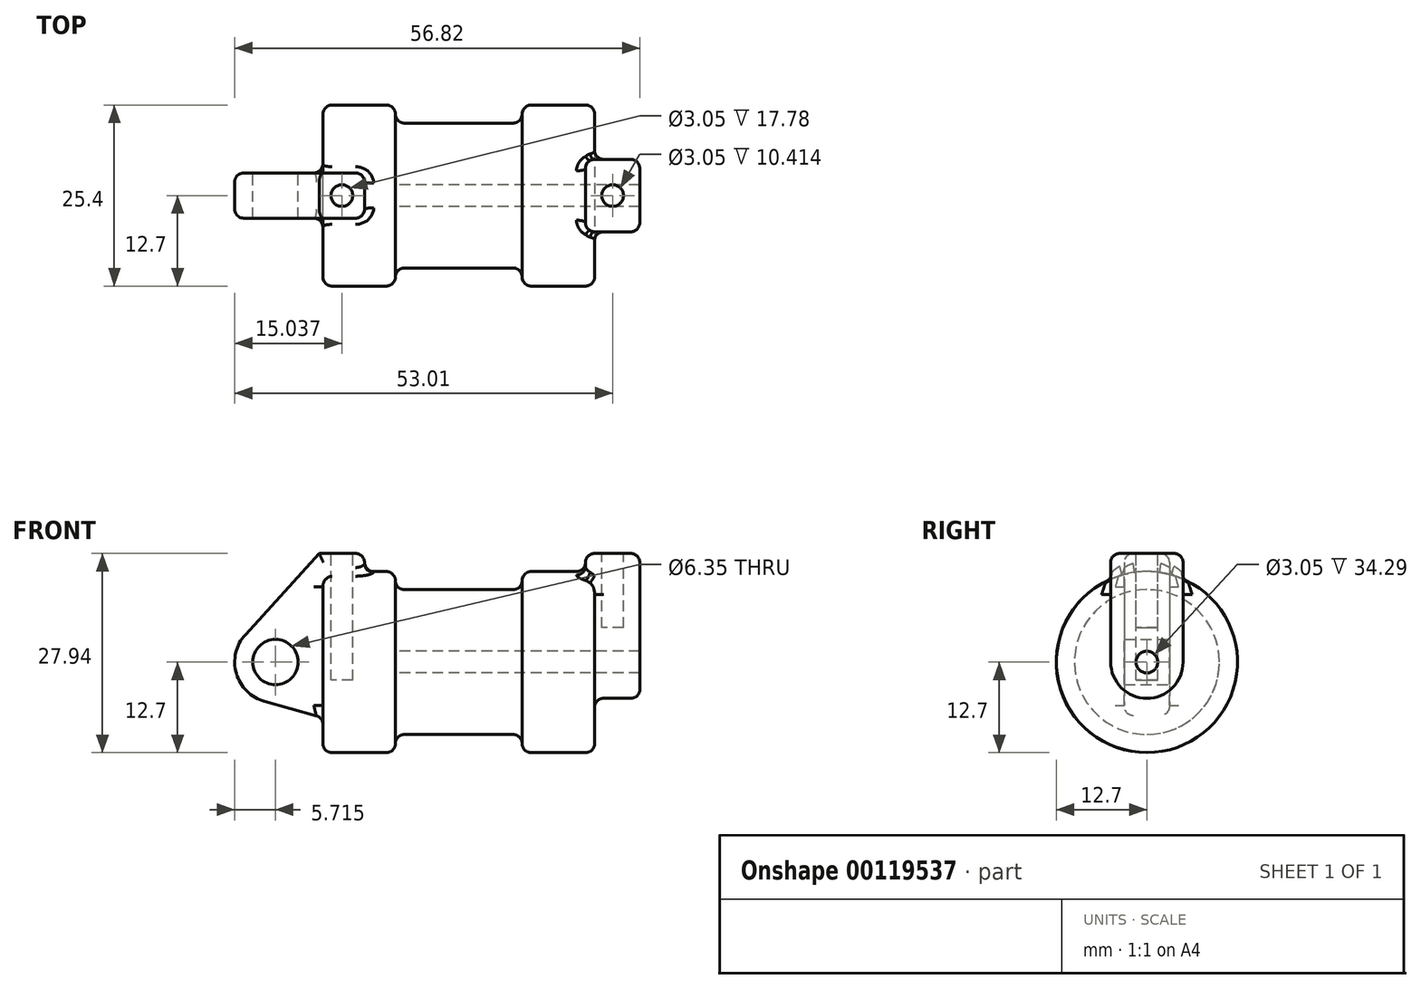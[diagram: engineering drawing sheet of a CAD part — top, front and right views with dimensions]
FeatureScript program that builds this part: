
annotation { "Feature Type Name" : "Feature", "Feature Type Description" : "" }
export const myFeature = defineFeature(function(context is Context, id is Id, definition is map)
    precondition{}
    {
        {
            var Q0;
            Q0=qCreatedBy(makeId("Front.planeOp"),FACE);
            var sketch = newSketch(context, id + "F0", { "sketchPlane" : qUnion([Q0])});
            skLineSegment(sketch, "E0", {"start": v(0, 0) * mm, "end": v(0, 12.7) * mm});
            skLineSegment(sketch, "E1", {"start": v(0, 12.7) * mm, "end": v(10.16, 12.7) * mm});
            skLineSegment(sketch, "E2", {"start": v(10.16, 12.7) * mm, "end": v(10.16, 10.16) * mm});
            skLineSegment(sketch, "E3", {"start": v(10.16, 10.16) * mm, "end": v(27.94, 10.16) * mm});
            skLineSegment(sketch, "E4", {"start": v(27.94, 10.16) * mm, "end": v(27.94, 12.7) * mm});
            skLineSegment(sketch, "E5", {"start": v(27.94, 12.7) * mm, "end": v(38.1, 12.7) * mm});
            skLineSegment(sketch, "E6", {"start": v(38.1, 12.7) * mm, "end": v(38.1, 0) * mm});
            skLineSegment(sketch, "E7", {"start": v(38.1, 0) * mm, "end": v(0, 0) * mm});
            skLineSegment(sketch, "E8", {"start": v(5.84, 15.24) * mm, "end": v(-0.5, 15.24) * mm});
            skLineSegment(sketch, "E9", {"start": v(-0.5, 15.24) * mm, "end": v(-10.88, 3.85) * mm});
            skLineSegment(sketch, "E10", {"start": v(0, 0) * mm, "end": v(-6.65, 0) * mm});
            skCircle(sketch, "E11", {"center": v(-6.65, 0) * mm, "radius": 5.72 * mm});
            skCircle(sketch, "E12", {"center": v(-6.65, 0) * mm, "radius": 3.18 * mm});
            skLineSegment(sketch, "E13", {"start": v(5.84, 15.24) * mm, "end": v(5.84, -9.4) * mm});
            skLineSegment(sketch, "E14", {"start": v(5.84, -9.4) * mm, "end": v(-8.18, -5.5) * mm});
            skSolve(sketch);
        }
        {
            var Q0;
            {var subQ0=sQuery(id+"F0.wireOp",EDGE,"E0");Q0=makeQuery(id+"F0.imprint","IMPRINT",FACE,{"disambiguationData":[TD([[makeQuery(id+"F0.imprint","IMPRINT",EDGE,{"derivedFrom":subQ0}),-1.0]])]});}
            var Q1;
            {var subQ0=sQuery(id+"F0.wireOp",EDGE,"E2");Q1=makeQuery(id+"F0.imprint","IMPRINT",FACE,{"disambiguationData":[TD([[makeQuery(id+"F0.imprint","IMPRINT",EDGE,{"derivedFrom":subQ0}),-1.0]])]});}
            var Q2;
            Q2=sQuery(id+"F0.wireOp",EDGE,"E7");
            revolve(context, id + "F1", {"entities" : qUnion([Q0, Q1]), "axis" : qUnion([Q2]), "revolveType" : RevolveType.FULL});
        }
        {
            var Q0;
            {var subQ4=sQuery(id+"F0.wireOp",EDGE,"E12");Q0=makeQuery(id+"F0.imprint","IMPRINT",FACE,{"disambiguationData":[TD([[makeQuery(id+"F0.imprint","IMPRINT",EDGE,{"derivedFrom":subQ4}),-1.0]])]});}
            var Q1;
            {var subQ0=sQuery(id+"F0.wireOp",EDGE,"E14");Q1=makeQuery(id+"F0.imprint","IMPRINT",FACE,{"disambiguationData":[TD([[makeQuery(id+"F0.imprint","IMPRINT",EDGE,{"derivedFrom":subQ0}),-1.0]])]});}
            var Q2;
            {var subQ3=sQuery(id+"F0.wireOp",EDGE,"E0");Q2=makeQuery(id+"F0.imprint","IMPRINT",FACE,{"disambiguationData":[TD([[makeQuery(id+"F0.imprint","IMPRINT",EDGE,{"derivedFrom":subQ3}),1.0]])]});}
            var Q3;
            {var subQ0=sQuery(id+"F0.wireOp",EDGE,"E0");Q3=makeQuery(id+"F0.imprint","IMPRINT",FACE,{"disambiguationData":[TD([[makeQuery(id+"F0.imprint","IMPRINT",EDGE,{"derivedFrom":subQ0}),-1.0]])]});}
            extrude(context, id + "F2", {"entities" : qUnion([Q0, Q1, Q2, Q3]), "operationType" : NewBodyOperationType.ADD, "endBound" : BoundingType.SYMMETRIC, "depth" : 6.35 * mm});
        }
        {
            var Q0;
            Q0=makeQuery(id+"F1.opRevolve","SWEPT_FACE",FACE,{"disambiguationData":[OSD([sQuery(id+"F0.wireOp",EDGE,"E6")])]});
            var sketch = newSketch(context, id + "F3", { "sketchPlane" : qUnion([Q0])});
            skCircle(sketch, "E15", {"center": v(0, 0) * mm, "radius": 1.52 * mm});
            skCircle(sketch, "E16", {"center": v(0, 0) * mm, "radius": 5.08 * mm});
            skLineSegment(sketch, "E17", {"start": v(-5.08, 0) * mm, "end": v(-5.08, 15.24) * mm});
            skLineSegment(sketch, "E18", {"start": v(-5.08, 15.24) * mm, "end": v(5.08, 15.24) * mm});
            skLineSegment(sketch, "E19", {"start": v(5.08, 15.24) * mm, "end": v(5.08, 0) * mm});
            skSolve(sketch);
        }
        {
            var Q0;
            {var subQ0=sQuery(id+"F3.wireOp",EDGE,"E18");Q0=makeQuery(id+"F3.imprint","IMPRINT",FACE,{"disambiguationData":[TD([[makeQuery(id+"F3.imprint","IMPRINT",EDGE,{"derivedFrom":subQ0}),-1.0]])]});}
            var Q1;
            {var subQ0=sQuery(id+"F3.wireOp",EDGE,"E17");var subQ1=sQuery(id+"F3.wireOp",EDGE,"E16");var subQ2=makeQuery(id+"F3.imprint","INTERSECT",VERTEX,{"derivedFrom":[subQ1,subQ0]});Q1=makeQuery(id+"F3.imprint","IMPRINT",FACE,{"disambiguationData":[TD([[makeQuery(id+"F3.imprint","IMPRINT",EDGE,{"disambiguationData":[TD([[subQ2,1.0]])],"derivedFrom":subQ1}),-1.0]])]});}
            var Q2;
            Q2=makeQuery(id+"F3.imprint","IMPRINT",FACE,{"disambiguationData":[TD([[makeQuery(id+"F3.imprint","IMPRINT",EDGE,{"derivedFrom":sQuery(id+"F3.wireOp",EDGE,"E15")}),-1.0]])]});
            extrude(context, id + "F4", {"entities" : qUnion([Q0, Q1, Q2]), "operationType" : NewBodyOperationType.ADD, "depth" : 6.35 * mm, "hasSecondDirection" : true, "secondDirectionOppositeDirection" : true, "secondDirectionDepth" : 1.27 * mm});
        }
        {
            var Q0;
            Q0=makeQuery(id+"F4.boolean.opBoolean","SPLIT",FACE,{"disambiguationData":[TD([makeQuery(id+"F4.opExtrude","SWEPT_FACE",FACE,{"disambiguationData":[OSD([sQuery(id+"F3.wireOp",EDGE,"E15")])]})])],"derivedFrom":makeQuery(id+"F1.opRevolve","SWEPT_FACE",FACE,{"disambiguationData":[OSD([sQuery(id+"F0.wireOp",EDGE,"E6")])]})});
            var Q1;
            Q1=makeQuery(id+"F1.opRevolve","SWEPT_FACE",FACE,{"disambiguationData":[OSD([sQuery(id+"F0.wireOp",EDGE,"E2")])]});
            extrude(context, id + "F5", {"entities" : qUnion([Q0]), "operationType" : NewBodyOperationType.REMOVE, "endBound" : BoundingType.UP_TO_SURFACE, "oppositeDirection" : true, "endBoundEntityFace" : qUnion([Q1]), "depth" : 25.4 * mm});
        }
        {
            var Q0;
            Q0=makeQuery(id+"F2.opExtrude","SWEPT_FACE",FACE,{"disambiguationData":[OSD([sQuery(id+"F0.wireOp",EDGE,"E8")])]});
            var sketch = newSketch(context, id + "F6", { "sketchPlane" : qUnion([Q0])});
            skLineSegment(sketch, "E20", {"start": v(2.67, 3.18) * mm, "end": v(2.67, -3.18) * mm, "construction": true});
            skLineSegment(sketch, "E21", {"start": v(-0.5, 0) * mm, "end": v(5.84, 0) * mm, "construction": true});
            skCircle(sketch, "E22", {"center": v(2.67, 0) * mm, "radius": 1.52 * mm});
            skSolve(sketch);
        }
        {
            var Q0;
            Q0=makeQuery(id+"F4.opExtrude","SWEPT_FACE",FACE,{"disambiguationData":[OSD([sQuery(id+"F3.wireOp",EDGE,"E18")])]});
            var sketch = newSketch(context, id + "F7", { "sketchPlane" : qUnion([Q0])});
            skLineSegment(sketch, "E23", {"start": v(40.64, 5.08) * mm, "end": v(40.64, -5.08) * mm, "construction": true});
            skLineSegment(sketch, "E24", {"start": v(36.83, 0) * mm, "end": v(44.45, 0) * mm, "construction": true});
            skCircle(sketch, "E25", {"center": v(40.64, 0) * mm, "radius": 1.52 * mm});
            skSolve(sketch);
        }
        {
            var Q0;
            Q0=makeQuery(id+"F6.imprint","IMPRINT",FACE,{"disambiguationData":[TD([[makeQuery(id+"F6.imprint","IMPRINT",EDGE,{"derivedFrom":sQuery(id+"F6.wireOp",EDGE,"E22")}),1.0]])]});
            extrude(context, id + "F8", {"entities" : qUnion([Q0]), "operationType" : NewBodyOperationType.REMOVE, "oppositeDirection" : true, "depth" : 17.78 * mm});
        }
        {
            var Q0;
            Q0=makeQuery(id+"F7.imprint","IMPRINT",FACE,{"disambiguationData":[TD([[makeQuery(id+"F7.imprint","IMPRINT",EDGE,{"derivedFrom":sQuery(id+"F7.wireOp",EDGE,"E25")}),1.0]])]});
            var Q1;
            Q1=sQuery(id+"F7.wireOp",EDGE,"E25");
            extrude(context, id + "F9", {"entities" : qUnion([Q0]), "operationType" : NewBodyOperationType.REMOVE, "surfaceEntities" : qUnion([Q1]), "oppositeDirection" : true, "depth" : 10.4 * mm});
        }
        {
            var Q0;
            Q0=makeQuery(id+"F1.opRevolve","SWEPT_EDGE",EDGE,{"disambiguationData":[OSD([sQuery(id+"F0.wireOp",EDGE,"E4"),sQuery(id+"F0.wireOp",EDGE,"E5")])]});
            var Q1;
            Q1=makeQuery(id+"F1.opRevolve","SWEPT_EDGE",EDGE,{"disambiguationData":[OSD([sQuery(id+"F0.wireOp",EDGE,"E1"),sQuery(id+"F0.wireOp",EDGE,"E2")])]});
            fillet(context, id + "F10", {"entities" : qUnion([Q0, Q1]), "radius" : 1.27 * mm, "tangentPropagation" : true, "allowEdgeOverflow" : false});
        }
        {
            var Q0;
            Q0=makeQuery(id+"F1.opRevolve","SWEPT_EDGE",EDGE,{"disambiguationData":[OSD([sQuery(id+"F0.wireOp",EDGE,"E3"),sQuery(id+"F0.wireOp",EDGE,"E4")])]});
            var Q1;
            Q1=makeQuery(id+"F1.opRevolve","SWEPT_EDGE",EDGE,{"disambiguationData":[OSD([sQuery(id+"F0.wireOp",EDGE,"E2"),sQuery(id+"F0.wireOp",EDGE,"E3")])]});
            fillet(context, id + "F11", {"entities" : qUnion([Q0, Q1]), "radius" : 1.27 * mm, "tangentPropagation" : true, "allowEdgeOverflow" : false});
        }
        {
            var Q0;
            Q0=makeQuery(id+"F1.opRevolve","SWEPT_EDGE",EDGE,{"disambiguationData":[OSD([sQuery(id+"F0.wireOp",EDGE,"E5"),sQuery(id+"F0.wireOp",EDGE,"E6")])]});
            fillet(context, id + "F12", {"entities" : qUnion([Q0]), "radius" : 1.27 * mm, "tangentPropagation" : true, "allowEdgeOverflow" : false});
        }
        {
            var Q0;
            Q0=makeQuery(id+"F1.opRevolve","SWEPT_EDGE",EDGE,{"disambiguationData":[OSD([sQuery(id+"F0.wireOp",EDGE,"E0"),sQuery(id+"F0.wireOp",EDGE,"E1")])]});
            fillet(context, id + "F13", {"entities" : qUnion([Q0]), "radius" : 1.27 * mm, "tangentPropagation" : true, "allowEdgeOverflow" : false});
        }
        {
            var Q0;
            Q0=makeQuery(id+"F4.opExtrude","CAP_EDGE",EDGE,{"disambiguationData":[OSD([sQuery(id+"F3.wireOp",EDGE,"E19")])],"isStart":false});
            var Q1;
            Q1=makeQuery(id+"F4.opExtrude","CAP_EDGE",EDGE,{"disambiguationData":[OSD([sQuery(id+"F3.wireOp",EDGE,"E16")])],"isStart":false});
            var Q2;
            Q2=makeQuery(id+"F4.opExtrude","CAP_EDGE",EDGE,{"disambiguationData":[OSD([sQuery(id+"F3.wireOp",EDGE,"E17")])],"isStart":false});
            var Q3;
            Q3=makeQuery(id+"F4.opExtrude","SWEPT_EDGE",EDGE,{"disambiguationData":[OSD([sQuery(id+"F3.wireOp",EDGE,"E17"),sQuery(id+"F3.wireOp",EDGE,"E18")])]});
            var Q4;
            Q4=makeQuery(id+"F4.opExtrude","CAP_EDGE",EDGE,{"disambiguationData":[OSD([sQuery(id+"F3.wireOp",EDGE,"E18")])],"isStart":false});
            var Q5;
            Q5=makeQuery(id+"F4.opExtrude","SWEPT_EDGE",EDGE,{"disambiguationData":[OSD([sQuery(id+"F3.wireOp",EDGE,"E18"),sQuery(id+"F3.wireOp",EDGE,"E19")])]});
            var Q6;
            Q6=makeQuery(id+"F4.opExtrude","CAP_EDGE",EDGE,{"disambiguationData":[OSD([sQuery(id+"F3.wireOp",EDGE,"E18")])],"isStart":true});
            var Q7;
            Q7=makeQuery(id+"F4.opExtrude","CAP_EDGE",EDGE,{"disambiguationData":[OSD([sQuery(id+"F3.wireOp",EDGE,"E17")])],"isStart":true});
            var Q8;
            Q8=makeQuery(id+"F4.opExtrude","CAP_EDGE",EDGE,{"disambiguationData":[OSD([sQuery(id+"F3.wireOp",EDGE,"E19")])],"isStart":true});
            var Q9;
            Q9=makeQuery(id+"F4.opExtrude","SWEPT_EDGE",EDGE,{"disambiguationData":[OSD([sQuery(id+"F3.wireOp",EDGE,"E16"),sQuery(id+"F3.wireOp",EDGE,"E17")])]});
            fillet(context, id + "F14", {"entities" : qUnion([Q0, Q1, Q2, Q3, Q4, Q5, Q6, Q7, Q8, Q9]), "radius" : 1.27 * mm, "tangentPropagation" : true, "allowEdgeOverflow" : false});
        }
        {
            var Q0;
            Q0=makeQuery(id+"F4.boolean.opBoolean","INTERSECT",EDGE,{"derivedFrom":[makeQuery(id+"F1.opRevolve","SWEPT_FACE",FACE,{"disambiguationData":[OSD([sQuery(id+"F0.wireOp",EDGE,"E6")])]}),makeQuery(id+"F4.opExtrude","SWEPT_FACE",FACE,{"disambiguationData":[OSD([sQuery(id+"F3.wireOp",EDGE,"E19")])]})]});
            var Q1;
            Q1=makeQuery(id+"F4.boolean.opBoolean","INTERSECT",EDGE,{"derivedFrom":[makeQuery(id+"F1.opRevolve","SWEPT_FACE",FACE,{"disambiguationData":[OSD([sQuery(id+"F0.wireOp",EDGE,"E6")])]}),makeQuery(id+"F4.opExtrude","SWEPT_FACE",FACE,{"disambiguationData":[OSD([sQuery(id+"F3.wireOp",EDGE,"E16")])]})]});
            var Q2;
            Q2=makeQuery(id+"F4.boolean.opBoolean","INTERSECT",EDGE,{"derivedFrom":[makeQuery(id+"F1.opRevolve","SWEPT_FACE",FACE,{"disambiguationData":[OSD([sQuery(id+"F0.wireOp",EDGE,"E6")])]}),makeQuery(id+"F4.opExtrude","SWEPT_FACE",FACE,{"disambiguationData":[OSD([sQuery(id+"F3.wireOp",EDGE,"E17")])]})]});
            fillet(context, id + "F15", {"entities" : qUnion([Q0, Q1, Q2]), "radius" : 1.27 * mm, "tangentPropagation" : true, "allowEdgeOverflow" : false});
        }
        {
            var Q0;
            Q0=makeQuery(id+"F2.opExtrude","CAP_EDGE",EDGE,{"disambiguationData":[OSD([sQuery(id+"F0.wireOp",EDGE,"E8")])],"isStart":true});
            var Q1;
            Q1=makeQuery(id+"F2.opExtrude","CAP_EDGE",EDGE,{"disambiguationData":[OSD([sQuery(id+"F0.wireOp",EDGE,"E8")])],"isStart":false});
            var Q2;
            Q2=makeQuery(id+"F2.opExtrude","SWEPT_EDGE",EDGE,{"disambiguationData":[OSD([sQuery(id+"F0.wireOp",EDGE,"E8"),sQuery(id+"F0.wireOp",EDGE,"E13")])]});
            var Q3;
            Q3=makeQuery(id+"F2.boolean.opBoolean","INTERSECT",EDGE,{"derivedFrom":[makeQuery(id+"F1.opRevolve","SWEPT_FACE",FACE,{"disambiguationData":[OSD([sQuery(id+"F0.wireOp",EDGE,"E1")])]}),makeQuery(id+"F2.opExtrude","SWEPT_FACE",FACE,{"disambiguationData":[OSD([sQuery(id+"F0.wireOp",EDGE,"E13")])]})]});
            var Q4;
            Q4=makeQuery(id+"F2.boolean.opBoolean","INTERSECT",EDGE,{"derivedFrom":[makeQuery(id+"F1.opRevolve","SWEPT_FACE",FACE,{"disambiguationData":[OSD([sQuery(id+"F0.wireOp",EDGE,"E1")])]}),makeQuery(id+"F2.opExtrude","CAP_FACE",FACE,{"disambiguationData":[OSD([sQuery(id+"F0.wireOp",EDGE,"E8"),sQuery(id+"F0.wireOp",EDGE,"E9"),sQuery(id+"F0.wireOp",EDGE,"E11"),sQuery(id+"F0.wireOp",EDGE,"E12"),sQuery(id+"F0.wireOp",EDGE,"E13"),sQuery(id+"F0.wireOp",EDGE,"E14")])],"isStart":true})]});
            var Q5;
            Q5=makeQuery(id+"F2.boolean.opBoolean","INTERSECT",EDGE,{"derivedFrom":[makeQuery(id+"F1.opRevolve","SWEPT_FACE",FACE,{"disambiguationData":[OSD([sQuery(id+"F0.wireOp",EDGE,"E1")])]}),makeQuery(id+"F2.opExtrude","CAP_FACE",FACE,{"disambiguationData":[OSD([sQuery(id+"F0.wireOp",EDGE,"E8"),sQuery(id+"F0.wireOp",EDGE,"E9"),sQuery(id+"F0.wireOp",EDGE,"E11"),sQuery(id+"F0.wireOp",EDGE,"E12"),sQuery(id+"F0.wireOp",EDGE,"E13"),sQuery(id+"F0.wireOp",EDGE,"E14")])],"isStart":false})]});
            var Q6;
            Q6=makeQuery(id+"F1.opRevolve","SWEPT_FACE",FACE,{"disambiguationData":[OSD([sQuery(id+"F0.wireOp",EDGE,"E1")])]});
            var Q7;
            Q7=makeQuery(id+"F2.opExtrude","CAP_EDGE",EDGE,{"disambiguationData":[OSD([sQuery(id+"F0.wireOp",EDGE,"E13")])],"isStart":true});
            var Q8;
            Q8=makeQuery(id+"F2.opExtrude","CAP_EDGE",EDGE,{"disambiguationData":[OSD([sQuery(id+"F0.wireOp",EDGE,"E13")])],"isStart":false});
            var Q9;
            Q9=makeQuery(id+"F2.boolean.opBoolean","INTERSECT",EDGE,{"derivedFrom":[makeQuery(id+"F1.opRevolve","SWEPT_FACE",FACE,{"disambiguationData":[OSD([sQuery(id+"F0.wireOp",EDGE,"E0")])]}),makeQuery(id+"F2.opExtrude","SWEPT_FACE",FACE,{"disambiguationData":[OSD([sQuery(id+"F0.wireOp",EDGE,"E14")])]})]});
            var Q10;
            Q10=makeQuery(id+"F2.opExtrude","CAP_EDGE",EDGE,{"disambiguationData":[OSD([sQuery(id+"F0.wireOp",EDGE,"E14")])],"isStart":true});
            var Q11;
            Q11=makeQuery(id+"F2.opExtrude","CAP_EDGE",EDGE,{"disambiguationData":[OSD([sQuery(id+"F0.wireOp",EDGE,"E14")])],"isStart":false});
            fillet(context, id + "F16", {"entities" : qUnion([Q0, Q1, Q2, Q3, Q4, Q5, Q6, Q7, Q8, Q9, Q10, Q11]), "radius" : 1.27 * mm, "tangentPropagation" : true, "allowEdgeOverflow" : false});
        }
    });
